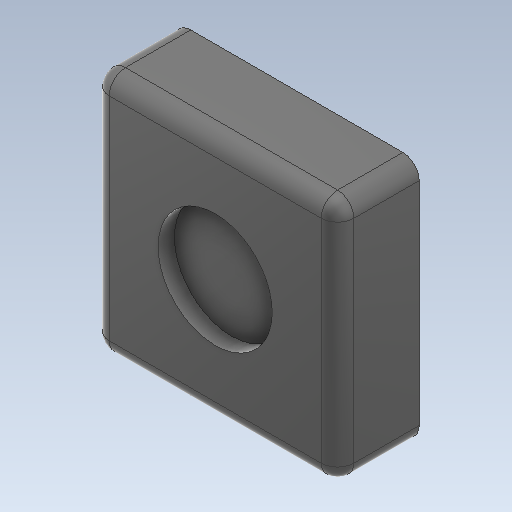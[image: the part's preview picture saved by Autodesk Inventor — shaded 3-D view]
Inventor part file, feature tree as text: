
AUTODESK INVENTOR PART (.ipt)
format: ipt  version: 2020 (Build 240168000, 168)  size: 139,776 bytes
history: native  units: mm
features: extrude x2, sketch x2, fillet x1
ambient origin geometry x8: Origin, YZ Plane, XZ Plane, XY Plane, X Axis, Y Axis, Z Axis, Center Point
bodies: Solid1 (feature_tree)
feature tree (5):
  extrude  "Extrusion1"  Depth=30.0mm
  extrude  "Extrusion2"  Depth=2.0mm
  fillet  "Fillet1"  Radius=2.0mm
  sketch  "Sketch1"  dims[d0=30.0mm d1=30.0mm]
  sketch  "Sketch2"  dims[d2=10.0mm d3=0.0mm d4=14.0mm d5=2.0mm d6=0.0mm d7=2.0mm]
